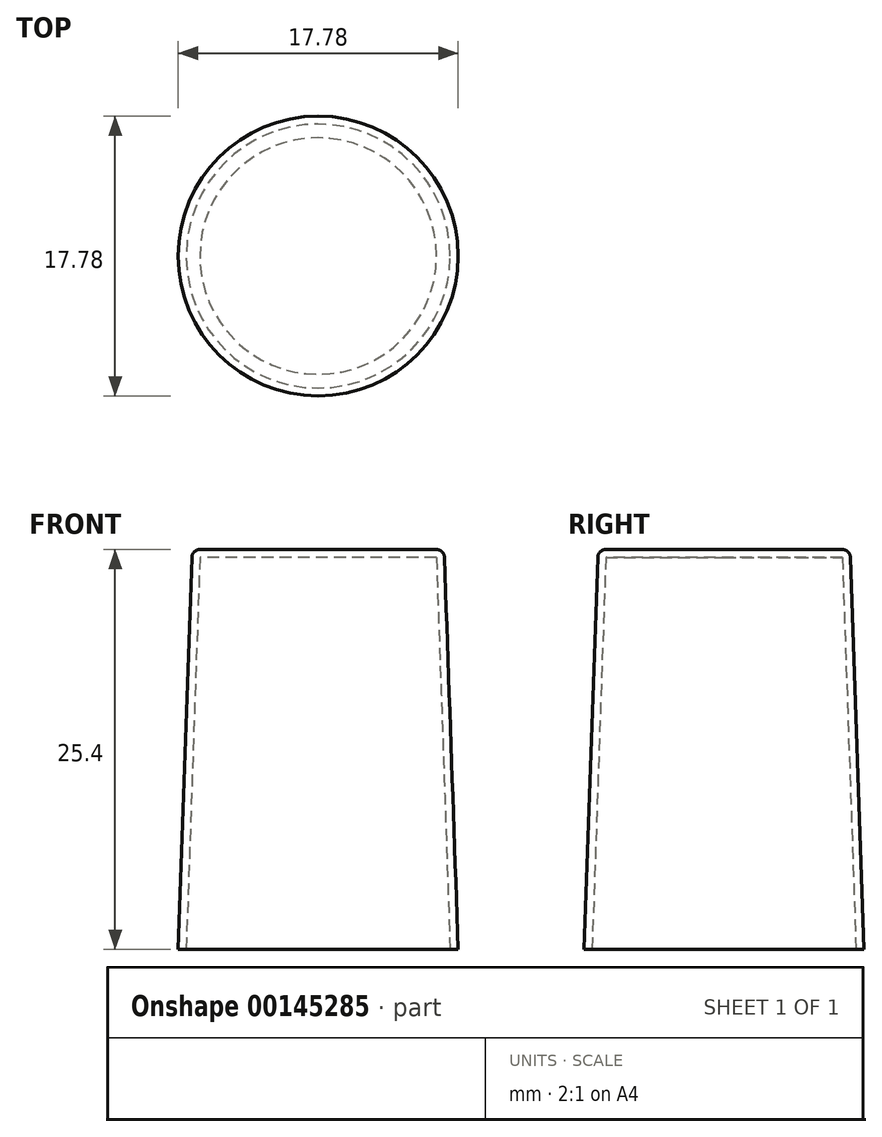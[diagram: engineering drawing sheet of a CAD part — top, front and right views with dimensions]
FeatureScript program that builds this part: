
annotation { "Feature Type Name" : "Feature", "Feature Type Description" : "" }
export const myFeature = defineFeature(function(context is Context, id is Id, definition is map)
    precondition{}
    {
        {
            var Q0;
            Q0=qCreatedBy(makeId("Top.planeOp"),FACE);
            var sketch = newSketch(context, id + "F0", { "sketchPlane" : qUnion([Q0])});
            skCircle(sketch, "E0", {"center": v(0, 0) * mm, "radius": 8.9 * mm});
            skSolve(sketch);
        }
        {
            var Q0;
            Q0=makeQuery(id+"F0.imprint","IMPRINT",FACE,{"disambiguationData":[TD([[makeQuery(id+"F0.imprint","IMPRINT",EDGE,{"derivedFrom":sQuery(id+"F0.wireOp",EDGE,"E0")}),1.0]])]});
            extrude(context, id + "F1", {"entities" : qUnion([Q0]), "depth" : 25.4 * mm, "hasDraft" : true, "draftAngle" : 2 * degree, "draftPullDirection" : true});
        }
        {
            var Q0;
            Q0=makeQuery(id+"F1.opExtrude","CAP_FACE",FACE,{"disambiguationData":[OSD([sQuery(id+"F0.wireOp",EDGE,"E0")])],"isStart":true});
            shell(context, id + "F2", {"entities" : qUnion([Q0]), "thickness" : 0.5 * mm});
        }
        {
            var Q0;
            Q0=makeQuery(id+"F1.opExtrude","CAP_EDGE",EDGE,{"disambiguationData":[OSD([sQuery(id+"F0.wireOp",EDGE,"E0")])],"isStart":false});
            fillet(context, id + "F3", {"entities" : qUnion([Q0]), "radius" : 0.5 * mm, "tangentPropagation" : true, "allowEdgeOverflow" : false});
        }
    });
